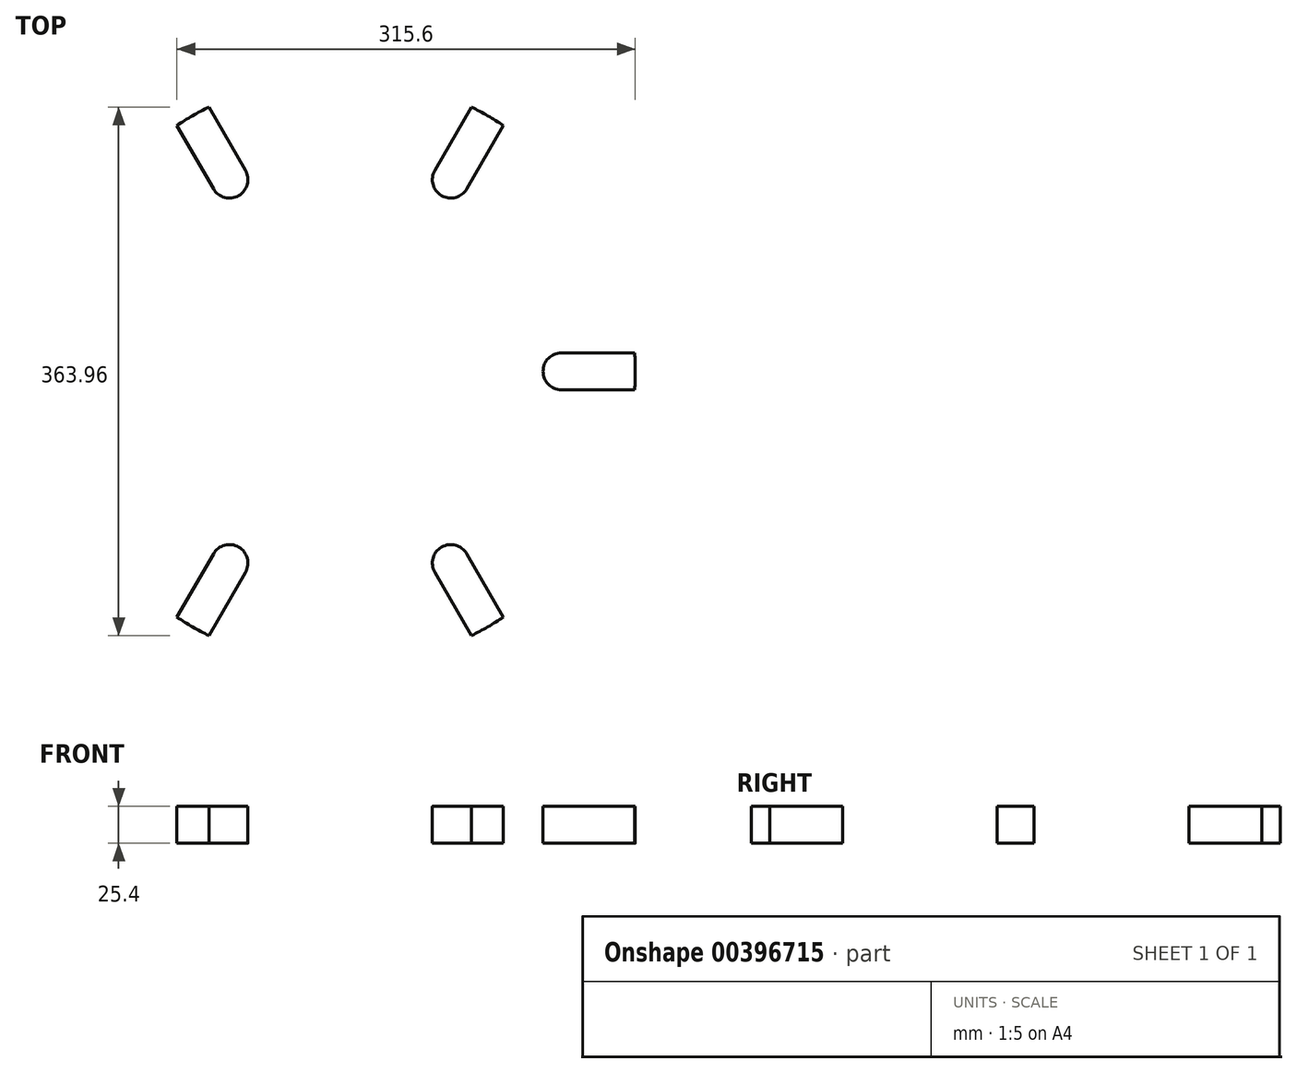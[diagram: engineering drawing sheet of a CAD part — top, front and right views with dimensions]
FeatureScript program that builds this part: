
annotation { "Feature Type Name" : "Feature", "Feature Type Description" : "" }
export const myFeature = defineFeature(function(context is Context, id is Id, definition is map)
    precondition{}
    {
        {
            var Q0;
            Q0=qCreatedBy(makeId("Top.planeOp"),FACE);
            var sketch = newSketch(context, id + "F0", { "sketchPlane" : qUnion([Q0])});
            skCircle(sketch, "E0", {"center": v(0, 0) * mm, "radius": 203.2 * mm});
            skSolve(sketch);
        }
        {
            var Q0;
            Q0=makeQuery(id+"F0.imprint","IMPRINT",FACE,{"disambiguationData":[TD([[makeQuery(id+"F0.imprint","IMPRINT",EDGE,{"derivedFrom":sQuery(id+"F0.wireOp",EDGE,"E0")}),1.0]])]});
            extrude(context, id + "F1", {"entities" : qUnion([Q0]), "depth" : 25.4 * mm});
        }
        {
            var Q0;
            Q0=makeQuery(id+"F1.opExtrude","CAP_FACE",FACE,{"disambiguationData":[OSD([sQuery(id+"F0.wireOp",EDGE,"E0")])],"isStart":false});
            var sketch = newSketch(context, id + "F2", { "sketchPlane" : qUnion([Q0])});
            skLineSegment(sketch, "E1", {"start": v(-203.2, 0) * mm, "end": v(-152.4, 0) * mm});
            skArc(sketch, "E2.0.startCap", {"start": v(-203.2, -12.7) * mm, "mid": v(-215.9, 0) * mm, "end": v(-203.2, 12.7) * mm});
            skArc(sketch, "E2.0.endCap", {"start": v(-152.4, 12.7) * mm, "mid": v(-139.7, 0) * mm, "end": v(-152.4, -12.7) * mm});
            skLineSegment(sketch, "E2.0.left", {"start": v(-203.2, 12.7) * mm, "end": v(-152.4, 12.7) * mm});
            skLineSegment(sketch, "E2.0.right", {"start": v(-203.2, -12.7) * mm, "end": v(-152.4, -12.7) * mm});
            skLineSegment(sketch, "E3.1.0", {"start": v(-112.6, -169.63) * mm, "end": v(-87.2, -125.63) * mm});
            skArc(sketch, "E3.1.1", {"start": v(-87.2, -125.63) * mm, "mid": v(-69.85, -120.98) * mm, "end": v(-65.2, -138.33) * mm});
            skLineSegment(sketch, "E3.1.2", {"start": v(-90.6, -182.33) * mm, "end": v(-65.2, -138.33) * mm});
            skLineSegment(sketch, "E3.2.0", {"start": v(90.6, -182.33) * mm, "end": v(65.2, -138.33) * mm});
            skArc(sketch, "E3.2.1", {"start": v(65.2, -138.33) * mm, "mid": v(69.85, -120.98) * mm, "end": v(87.2, -125.63) * mm});
            skLineSegment(sketch, "E3.2.2", {"start": v(112.6, -169.63) * mm, "end": v(87.2, -125.63) * mm});
            skPoint(sketch, "E3.center", {"position": v(0, 0) * mm});
            skLineSegment(sketch, "E4.1.3.0", {"start": v(203.2, -12.7) * mm, "end": v(152.4, -12.7) * mm});
            skArc(sketch, "E4.3.3.0", {"start": v(152.4, -12.7) * mm, "mid": v(139.7, 0) * mm, "end": v(152.4, 12.7) * mm});
            skLineSegment(sketch, "E4.7.3.0", {"start": v(203.2, 12.7) * mm, "end": v(152.4, 12.7) * mm});
            skLineSegment(sketch, "E4.1.4.0", {"start": v(112.6, 169.63) * mm, "end": v(87.2, 125.63) * mm});
            skArc(sketch, "E4.3.4.0", {"start": v(87.2, 125.63) * mm, "mid": v(69.85, 120.98) * mm, "end": v(65.2, 138.33) * mm});
            skLineSegment(sketch, "E4.7.4.0", {"start": v(90.6, 182.33) * mm, "end": v(65.2, 138.33) * mm});
            skLineSegment(sketch, "E4.1.5.0", {"start": v(-90.6, 182.33) * mm, "end": v(-65.2, 138.33) * mm});
            skArc(sketch, "E4.3.5.0", {"start": v(-65.2, 138.33) * mm, "mid": v(-69.85, 120.98) * mm, "end": v(-87.2, 125.63) * mm});
            skLineSegment(sketch, "E4.7.5.0", {"start": v(-112.6, 169.63) * mm, "end": v(-87.2, 125.63) * mm});
            skSolve(sketch);
        }
        {
            var Q0;
            Q0 = qSketchRegion(id + "F2", true);
            var Q1;
            {var subQ0=sQuery(id+"F2.wireOp",EDGE,"E3.1.1");Q1=makeQuery(id+"F2.imprint","IMPRINT",FACE,{"disambiguationData":[TD([[makeQuery(id+"F2.imprint","IMPRINT",EDGE,{"derivedFrom":subQ0}),-1.0]])]});}
            var Q2;
            {var subQ0=sQuery(id+"F2.wireOp",EDGE,"E3.2.1");Q2=makeQuery(id+"F2.imprint","IMPRINT",FACE,{"disambiguationData":[TD([[makeQuery(id+"F2.imprint","IMPRINT",EDGE,{"derivedFrom":subQ0}),-1.0]])]});}
            var Q3;
            {var subQ0=sQuery(id+"F2.wireOp",EDGE,"E4.3.3.0");Q3=makeQuery(id+"F2.imprint","IMPRINT",FACE,{"disambiguationData":[TD([[makeQuery(id+"F2.imprint","IMPRINT",EDGE,{"derivedFrom":subQ0}),-1.0]])]});}
            var Q4;
            {var subQ0=sQuery(id+"F2.wireOp",EDGE,"E4.3.4.0");Q4=makeQuery(id+"F2.imprint","IMPRINT",FACE,{"disambiguationData":[TD([[makeQuery(id+"F2.imprint","IMPRINT",EDGE,{"derivedFrom":subQ0}),-1.0]])]});}
            var Q5;
            {var subQ0=sQuery(id+"F2.wireOp",EDGE,"E4.3.5.0");Q5=makeQuery(id+"F2.imprint","IMPRINT",FACE,{"disambiguationData":[TD([[makeQuery(id+"F2.imprint","IMPRINT",EDGE,{"derivedFrom":subQ0}),-1.0]])]});}
            extrude(context, id + "F3", {"entities" : qUnion([Q0, Q1, Q2, Q3, Q4, Q5]), "operationType" : NewBodyOperationType.REMOVE, "endBound" : BoundingType.THROUGH_ALL, "oppositeDirection" : true, "depth" : 25.4 * mm});
        }
        {
            var Q0;
            Q0=makeQuery(id+"F1.opExtrude","CAP_FACE",FACE,{"disambiguationData":[OSD([sQuery(id+"F0.wireOp",EDGE,"E0")])],"isStart":false});
            var sketch = newSketch(context, id + "F4", { "sketchPlane" : qUnion([Q0])});
            skCircle(sketch, "E5", {"center": v(-152.4, 0) * mm, "radius": 44.45 * mm});
            skCircle(sketch, "E6.1.0", {"center": v(-76.2, -131.98) * mm, "radius": 44.45 * mm});
            skCircle(sketch, "E6.2.0", {"center": v(76.2, -131.98) * mm, "radius": 44.45 * mm});
            skPoint(sketch, "E6.center", {"position": v(0, 0) * mm});
            skCircle(sketch, "E7.1.3.0", {"center": v(152.4, 0) * mm, "radius": 44.45 * mm});
            skCircle(sketch, "E7.1.4.0", {"center": v(76.2, 131.98) * mm, "radius": 44.45 * mm});
            skCircle(sketch, "E7.1.5.0", {"center": v(-76.2, 131.98) * mm, "radius": 44.45 * mm});
            skCircle(sketch, "E8", {"center": v(0, 0) * mm, "radius": 88.9 * mm});
            skCircle(sketch, "E9.cCircle", {"center": v(0, 0) * mm, "radius": 88.9 * mm, "construction": true});
            skLineSegment(sketch, "E9.0", {"start": v(0, 88.9) * mm, "end": v(25.05, 85.3) * mm});
            skLineSegment(sketch, "E9.1", {"start": v(25.05, 85.3) * mm, "end": v(48.06, 74.79) * mm});
            skLineSegment(sketch, "E9.2", {"start": v(48.06, 74.79) * mm, "end": v(67.19, 58.22) * mm});
            skLineSegment(sketch, "E9.3", {"start": v(67.19, 58.22) * mm, "end": v(80.87, 36.93) * mm});
            skLineSegment(sketch, "E9.4", {"start": v(80.87, 36.93) * mm, "end": v(88, 12.65) * mm});
            skLineSegment(sketch, "E9.5", {"start": v(88, 12.65) * mm, "end": v(88, -12.65) * mm});
            skLineSegment(sketch, "E9.6", {"start": v(88, -12.65) * mm, "end": v(80.87, -36.93) * mm});
            skLineSegment(sketch, "E9.7", {"start": v(80.87, -36.93) * mm, "end": v(67.19, -58.22) * mm});
            skLineSegment(sketch, "E9.8", {"start": v(67.19, -58.22) * mm, "end": v(48.06, -74.79) * mm});
            skLineSegment(sketch, "E9.9", {"start": v(48.06, -74.79) * mm, "end": v(25.05, -85.3) * mm});
            skLineSegment(sketch, "E9.10", {"start": v(25.05, -85.3) * mm, "end": v(0, -88.9) * mm});
            skLineSegment(sketch, "E9.11", {"start": v(0, -88.9) * mm, "end": v(-25.05, -85.3) * mm});
            skLineSegment(sketch, "E9.12", {"start": v(-25.05, -85.3) * mm, "end": v(-48.06, -74.79) * mm});
            skLineSegment(sketch, "E9.13", {"start": v(-48.06, -74.79) * mm, "end": v(-67.19, -58.22) * mm});
            skLineSegment(sketch, "E9.14", {"start": v(-67.19, -58.22) * mm, "end": v(-80.87, -36.93) * mm});
            skLineSegment(sketch, "E9.15", {"start": v(-80.87, -36.93) * mm, "end": v(-88, -12.65) * mm});
            skLineSegment(sketch, "E9.16", {"start": v(-88, -12.65) * mm, "end": v(-88, 12.65) * mm});
            skLineSegment(sketch, "E9.17", {"start": v(-88, 12.65) * mm, "end": v(-80.87, 36.93) * mm});
            skLineSegment(sketch, "E9.18", {"start": v(-80.87, 36.93) * mm, "end": v(-67.19, 58.22) * mm});
            skLineSegment(sketch, "E9.19", {"start": v(-67.19, 58.22) * mm, "end": v(-48.06, 74.79) * mm});
            skLineSegment(sketch, "E9.20", {"start": v(-48.06, 74.79) * mm, "end": v(-25.05, 85.3) * mm});
            skLineSegment(sketch, "E9.21", {"start": v(-25.05, 85.3) * mm, "end": v(0, 88.9) * mm});
            skCircle(sketch, "E10.0", {"center": v(0, 0) * mm, "radius": 76.2 * mm});
            skArc(sketch, "E11", {"start": v(25.05, 85.3) * mm, "mid": v(88.9, 0) * mm, "end": v(25.05, -85.3) * mm});
            skArc(sketch, "E12.0.startCap", {"start": v(23.26, 79.2) * mm, "mid": v(18.95, 87.09) * mm, "end": v(26.84, 91.4) * mm});
            skArc(sketch, "E12.0.endCap", {"start": v(26.84, -91.4) * mm, "mid": v(18.95, -87.09) * mm, "end": v(23.26, -79.2) * mm});
            skArc(sketch, "E12.0.left", {"start": v(26.84, 91.4) * mm, "mid": v(95.25, 0) * mm, "end": v(26.84, -91.4) * mm});
            skArc(sketch, "E12.0.right", {"start": v(23.26, 79.2) * mm, "mid": v(82.55, 0) * mm, "end": v(23.26, -79.2) * mm});
            skArc(sketch, "E13.MirrorCS", {"start": v(-26.84, 91.4) * mm, "mid": v(-95.25, 0) * mm, "end": v(-26.84, -91.4) * mm});
            skArc(sketch, "E14.MirrorCS", {"start": v(-26.84, -91.4) * mm, "mid": v(-18.95, -87.09) * mm, "end": v(-23.26, -79.2) * mm});
            skArc(sketch, "E15.MirrorCS", {"start": v(-23.26, 79.2) * mm, "mid": v(-82.55, 0) * mm, "end": v(-23.26, -79.2) * mm});
            skArc(sketch, "E16.MirrorCS", {"start": v(-23.26, 79.2) * mm, "mid": v(-18.95, 87.09) * mm, "end": v(-26.84, 91.4) * mm});
            skLineSegment(sketch, "E17", {"start": v(88, 12.65) * mm, "end": v(75.14, 12.65) * mm});
            skLineSegment(sketch, "E18.MirrorCS", {"start": v(88, -12.65) * mm, "end": v(75.14, -12.65) * mm});
            skLineSegment(sketch, "E19.MirrorCS", {"start": v(-88, 12.65) * mm, "end": v(-75.14, 12.65) * mm});
            skLineSegment(sketch, "E20.MirrorCS", {"start": v(-88, -12.65) * mm, "end": v(-75.14, -12.65) * mm});
            skSolve(sketch);
        }
        {
            var Q0;
            {var subQ0=sQuery(id+"F4.wireOp",EDGE,"E10.0");var subQ1=makeQuery(id+"F4.imprint","INTERSECT",VERTEX,{"derivedFrom":[subQ0,sQuery(id+"F4.wireOp",EDGE,"E17")]});Q0=makeQuery(id+"F4.imprint","IMPRINT",FACE,{"disambiguationData":[TD([[makeQuery(id+"F4.imprint","IMPRINT",EDGE,{"disambiguationData":[TD([[subQ1,-1.0]])],"derivedFrom":subQ0}),1.0]])]});}
            var Q1;
            {var subQ6=sQuery(id+"F4.wireOp",EDGE,"E9.17");Q1=makeQuery(id+"F4.imprint","IMPRINT",FACE,{"disambiguationData":[TD([[makeQuery(id+"F4.imprint","IMPRINT",EDGE,{"derivedFrom":subQ6}),-1.0]])]});}
            var Q2;
            {var subQ0=sQuery(id+"F4.wireOp",EDGE,"E9.16");Q2=makeQuery(id+"F4.imprint","IMPRINT",FACE,{"disambiguationData":[TD([[makeQuery(id+"F4.imprint","IMPRINT",EDGE,{"derivedFrom":subQ0}),-1.0]])]});}
            var Q3;
            {var subQ0=sQuery(id+"F4.wireOp",EDGE,"E19.MirrorCS");var subQ1=sQuery(id+"F4.wireOp",EDGE,"E10.0");var subQ2=makeQuery(id+"F4.imprint","INTERSECT",VERTEX,{"derivedFrom":[subQ1,subQ0]});Q3=makeQuery(id+"F4.imprint","IMPRINT",FACE,{"disambiguationData":[TD([[makeQuery(id+"F4.imprint","IMPRINT",EDGE,{"disambiguationData":[TD([[subQ2,-1.0]])],"derivedFrom":subQ1}),-1.0]])]});}
            var Q4;
            {var subQ0=sQuery(id+"F4.wireOp",EDGE,"E9.12");Q4=makeQuery(id+"F4.imprint","IMPRINT",FACE,{"disambiguationData":[TD([[makeQuery(id+"F4.imprint","IMPRINT",EDGE,{"derivedFrom":subQ0}),-1.0]])]});}
            var Q5;
            {var subQ2=sQuery(id+"F4.wireOp",EDGE,"E9.6");Q5=makeQuery(id+"F4.imprint","IMPRINT",FACE,{"disambiguationData":[TD([[makeQuery(id+"F4.imprint","IMPRINT",EDGE,{"derivedFrom":subQ2}),-1.0]])]});}
            var Q6;
            {var subQ0=sQuery(id+"F4.wireOp",EDGE,"E9.5");Q6=makeQuery(id+"F4.imprint","IMPRINT",FACE,{"disambiguationData":[TD([[makeQuery(id+"F4.imprint","IMPRINT",EDGE,{"derivedFrom":subQ0}),-1.0]])]});}
            var Q7;
            {var subQ0=sQuery(id+"F4.wireOp",EDGE,"E17");var subQ1=sQuery(id+"F4.wireOp",EDGE,"E10.0");var subQ2=makeQuery(id+"F4.imprint","INTERSECT",VERTEX,{"derivedFrom":[subQ1,subQ0]});Q7=makeQuery(id+"F4.imprint","IMPRINT",FACE,{"disambiguationData":[TD([[makeQuery(id+"F4.imprint","IMPRINT",EDGE,{"disambiguationData":[TD([[subQ2,1.0]])],"derivedFrom":subQ1}),-1.0]])]});}
            var Q8;
            {var subQ5=sQuery(id+"F4.wireOp",EDGE,"E9.1");Q8=makeQuery(id+"F4.imprint","IMPRINT",FACE,{"disambiguationData":[TD([[makeQuery(id+"F4.imprint","IMPRINT",EDGE,{"derivedFrom":subQ5}),-1.0]])]});}
            extrude(context, id + "F5", {"entities" : qUnion([Q0, Q1, Q2, Q3, Q4, Q5, Q6, Q7, Q8]), "operationType" : NewBodyOperationType.REMOVE, "endBound" : BoundingType.THROUGH_ALL, "oppositeDirection" : true, "depth" : 25.4 * mm});
        }
    });
